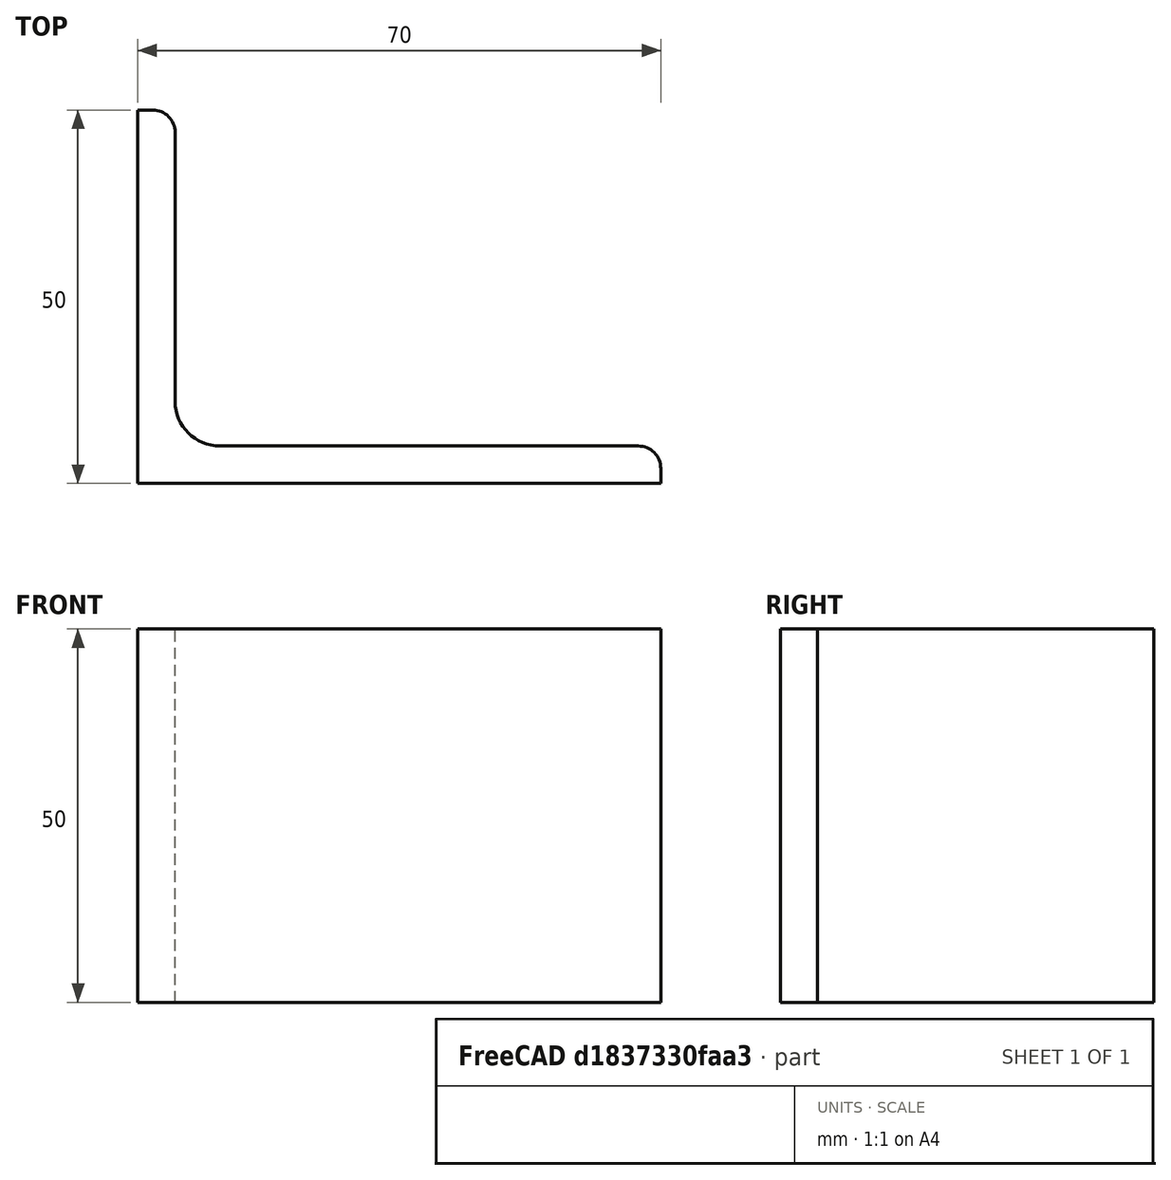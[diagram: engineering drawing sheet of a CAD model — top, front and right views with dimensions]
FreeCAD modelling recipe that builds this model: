
FCSTD DOCUMENT  (FreeCAD 0.15R4671 (Git))
Label: Angle Bar 70x50x5 EN10056 S235JR
License: All rights reserved
LicenseURL: http://en.wikipedia.org/wiki/All_rights_reserved
objects: Sketcher::SketchObject×1, Part::Extrusion×1
note: 2 computed .brp shape members not serialized (recipe doc carries the construction recipe); baked Part::Feature solids carry a one-line shape summary decoded from their .brp

FEATURE [Sketcher::SketchObject] Sketch
  sketch-geometry (9):
    g0: LineSegment StartX=0 StartY=0 StartZ=0 EndX=70 EndY=0 EndZ=0
    g1: LineSegment StartX=70 StartY=0 StartZ=0 EndX=70 EndY=2 EndZ=0
    g2: LineSegment StartX=67 StartY=5 StartZ=0 EndX=11 EndY=5 EndZ=0
    g3: LineSegment StartX=0 StartY=0 StartZ=0 EndX=0 EndY=50 EndZ=0
    g4: LineSegment StartX=0 StartY=50 StartZ=0 EndX=2 EndY=50 EndZ=0
    g5: LineSegment StartX=5 StartY=47 StartZ=0 EndX=5 EndY=11 EndZ=0
    g6: ArcOfCircle CenterX=11 CenterY=11 CenterZ=0 NormalX=0 NormalY=0 NormalZ=1 Radius=6 StartAngle=3.14159 EndAngle=4.71239
    g7: ArcOfCircle CenterX=2 CenterY=47 CenterZ=0 NormalX=0 NormalY=0 NormalZ=1 Radius=3 StartAngle=0 EndAngle=1.5708
    g8: ArcOfCircle CenterX=67 CenterY=2 CenterZ=0 NormalX=0 NormalY=0 NormalZ=1 Radius=3 StartAngle=0 EndAngle=1.5708
  constraints (23):
    c: Coincident(g0,g-1)
    c: Horizontal(g0)
    c: Coincident(g1,g0)
    c: Vertical(g1)
    c: Horizontal(g2)
    c: Coincident(g3,g-1)
    c: Vertical(g3)
    c: Coincident(g4,g3)
    c: Horizontal(g4)
    c: Vertical(g5)
    c: Tangent(g5,g6) = -1.5708
    c: Tangent(g2,g6) = 1.5708
    c: Tangent(g4,g7) = 1.5708
    c: Tangent(g5,g7) = 1.5708
    c: Tangent(g2,g8) = -1.5708
    c: Tangent(g1,g8) = -1.5708
    c: DistanceX(g0) = 70
    c: DistanceY(g3) = 50
    c: DistanceY(g0,g2) = 5
    c: DistanceX(g3,g5) = 5
    c: Radius(g6) = 6
    c: Radius(g8) = 3
    c: Radius(g7) = 3
FEATURE [Part::Extrusion] Extrude  label="Angle Bar 70x50x5 EN10056 S235JR"
  Base = -> Sketch
  Dir = (0,0,50)
  Solid = true
